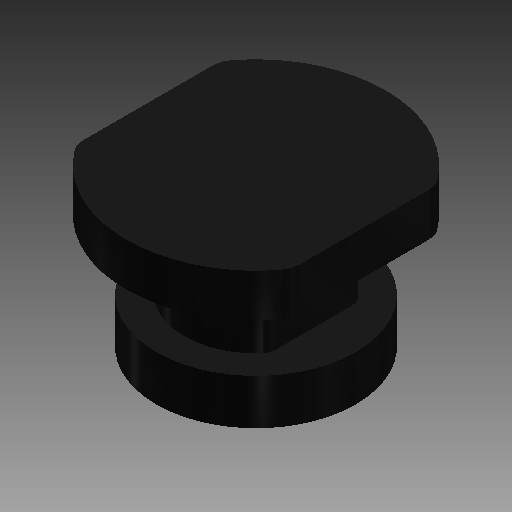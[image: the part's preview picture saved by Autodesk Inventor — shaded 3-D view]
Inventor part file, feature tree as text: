
AUTODESK INVENTOR PART (.ipt)
format: ipt  version: 2019 (Build 230136000, 136)  size: 136,704 bytes
history: native  units: mm
features: sketch x3, extrude x2, fillet x2, revolve x1
ambient origin geometry x8: Origin, YZ Plane, XZ Plane, XY Plane, X Axis, Y Axis, Z Axis, Center Point
bodies: Solid1 (feature_tree)
feature tree (8):
  revolve  "Revolution1"  [1 undecoded]
  extrude  "Extrusion1"  Depth=3.15mm
  extrude  "Extrusion2"  Depth=3.0mm
  fillet  "Fillet1"  [1 undecoded]
  fillet  "Fillet2"  Radius=15.0mm
  sketch  "Sketch1"  dims[d0=6.925mm d1=5.0mm]
  sketch  "Sketch2"  dims[d2=9.0mm d3=3.15mm]
  sketch  "Sketch3"  dims[d4=4.8mm d5=3.0mm d6=90.0deg d7=15.0mm d8=7.5mm d9=10.0mm d10=0.0mm d11=8.0mm d12=4.0mm d13=10.0mm d14=0.0mm d15=1.0mm d16=1.5mm]
note: 2 required parameter values undecoded (feature->parameter linkage not recoverable at this tier; creation-order binding heuristic only, values carry confidence <= 0.55)